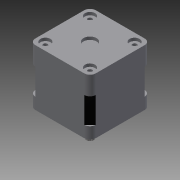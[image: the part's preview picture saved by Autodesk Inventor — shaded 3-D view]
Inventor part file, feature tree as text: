
AUTODESK INVENTOR PART (.ipt)
format: ipt  version: 2013 (Build 170138000, 138)  size: 202,240 bytes
history: native  units: mm
features: extrude x6, sketch x6, projected_geometry x4
ambient origin geometry x8: Origin, YZ Plane, XZ Plane, XY Plane, X Axis, Y Axis, Z Axis, Center Point
bodies: Solid1 (feature_tree)
feature tree (16):
  extrude  "Extrusion1"  Depth=18.0mm TaperAngle=0.0deg
  extrude  "Extrusion2"  Depth=7.0mm
  extrude  "Extrusion3"  Depth=7.0mm
  extrude  "Extrusion4"  Depth=2.0mm TaperAngle=0.0deg
  extrude  "Extrusion5"  Depth=15.5mm
  extrude  "Extrusion6"  Depth=2.0mm TaperAngle=0.0deg
  sketch  "Sketch1"  dims[d0=8.0mm d1=0.0mm d2=18.0mm d3=0.0mm]
  sketch  "Sketch2"  dims[d4=13.0mm d5=0.0mm d6=7.0mm]
  sketch  "Sketch3"  dims[d8=7.0mm d9=7.0mm]
  projected_geometry  "Projected Loop1"
  projected_geometry  "Projected Loop2"
  projected_geometry  "Projected Loop3"
  projected_geometry  "Projected Loop4"
  sketch  "Sketch4"  dims[d10=7.0mm d11=2.0mm d12=0.0mm]
  sketch  "Sketch5"  dims[d13=15.5mm d14=15.5mm]
  sketch  "Sketch6"  dims[d15=22.0mm d16=2.0mm d17=0.0mm d18=5.0mm d20=17.0mm d21=0.0mm d22=9.0mm d23=15.5mm d24=15.5mm]
